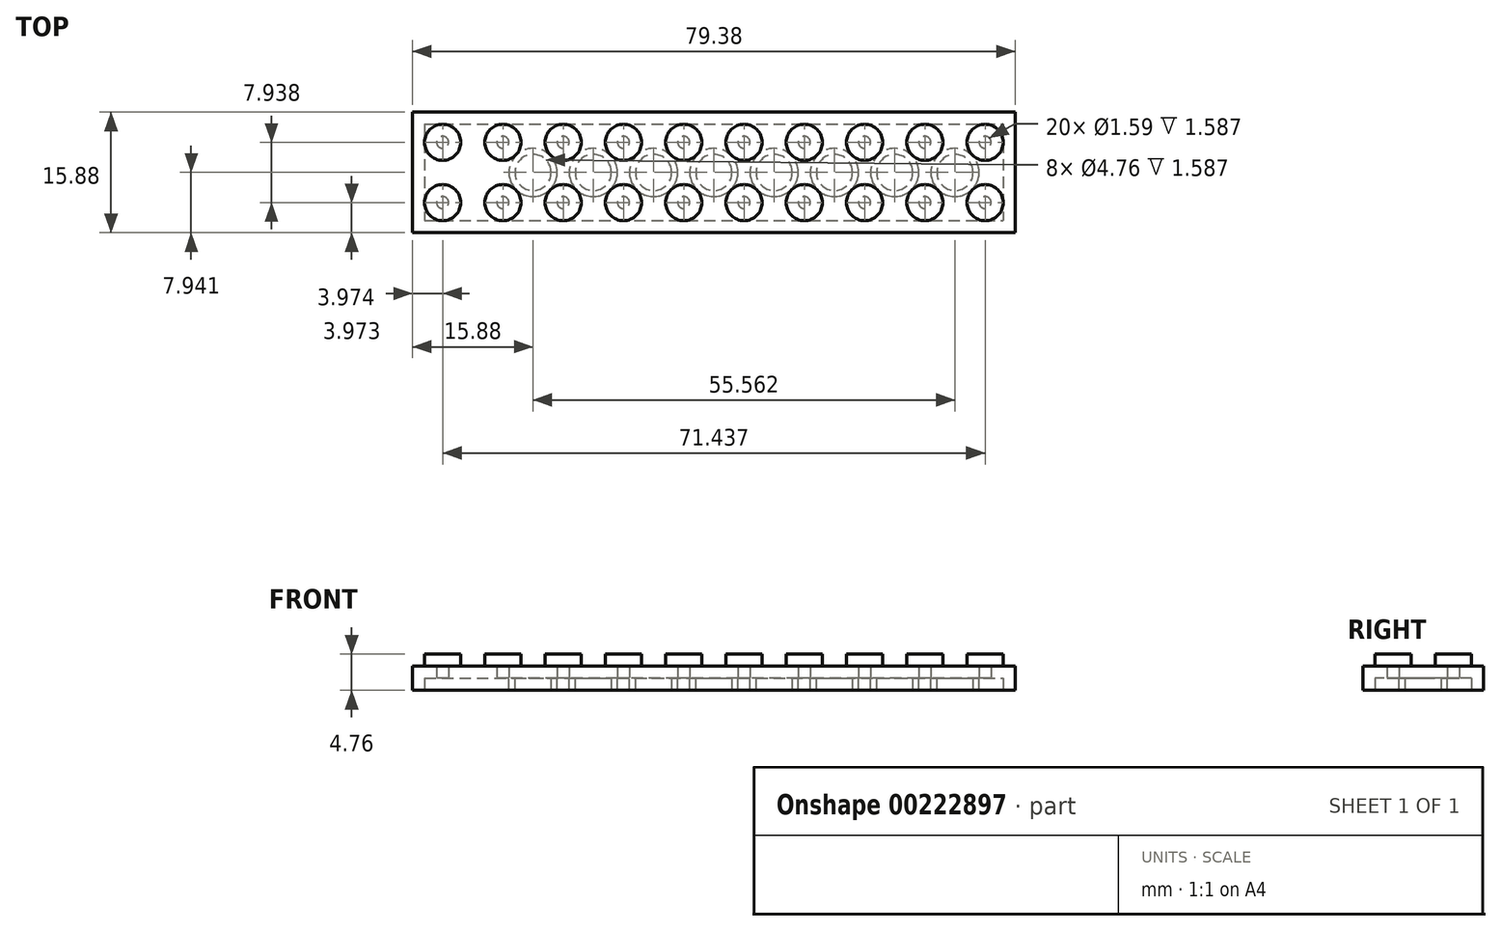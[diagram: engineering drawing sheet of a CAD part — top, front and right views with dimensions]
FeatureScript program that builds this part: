
annotation { "Feature Type Name" : "Feature", "Feature Type Description" : "" }
export const myFeature = defineFeature(function(context is Context, id is Id, definition is map)
    precondition{}
    {
        {
            var Q0;
            Q0=qCreatedBy(makeId("Top.planeOp"),FACE);
            var sketch = newSketch(context, id + "F0", { "sketchPlane" : qUnion([Q0])});
            skLineSegment(sketch, "E0.bottom", {"start": v(-15.88, 3.97) * mm, "end": v(63.5, 3.97) * mm});
            skLineSegment(sketch, "E0.top", {"start": v(-15.88, -11.9) * mm, "end": v(63.5, -11.9) * mm});
            skLineSegment(sketch, "E0.left", {"start": v(-15.88, 3.97) * mm, "end": v(-15.88, -11.9) * mm});
            skLineSegment(sketch, "E0.right", {"start": v(63.5, 3.97) * mm, "end": v(63.5, -11.9) * mm});
            skCircle(sketch, "E1", {"center": v(-11.9, 0) * mm, "radius": 2.38 * mm});
            skCircle(sketch, "E2.0.1.0", {"center": v(-11.9, -7.94) * mm, "radius": 2.38 * mm});
            skCircle(sketch, "E2.1.0.0", {"center": v(-3.97, 0) * mm, "radius": 2.38 * mm});
            skCircle(sketch, "E2.1.1.0", {"center": v(-3.97, -7.94) * mm, "radius": 2.38 * mm});
            skCircle(sketch, "E2.2.0.0", {"center": v(3.97, 0) * mm, "radius": 2.38 * mm});
            skCircle(sketch, "E2.2.1.0", {"center": v(3.97, -7.94) * mm, "radius": 2.38 * mm});
            skCircle(sketch, "E2.3.0.0", {"center": v(11.9, 0) * mm, "radius": 2.38 * mm});
            skCircle(sketch, "E2.3.1.0", {"center": v(11.9, -7.94) * mm, "radius": 2.38 * mm});
            skLineSegment(sketch, "E2.direction1", {"start": v(-11.9, 0) * mm, "end": v(-3.97, 0) * mm, "construction": true});
            skLineSegment(sketch, "E2.direction2", {"start": v(-11.9, 0) * mm, "end": v(-11.9, -7.94) * mm, "construction": true});
            skCircle(sketch, "E3.0.4.0", {"center": v(19.84, 0) * mm, "radius": 2.38 * mm});
            skCircle(sketch, "E3.0.4.1", {"center": v(19.84, -7.94) * mm, "radius": 2.38 * mm});
            skCircle(sketch, "E3.0.5.0", {"center": v(27.78, 0) * mm, "radius": 2.38 * mm});
            skCircle(sketch, "E3.0.5.1", {"center": v(27.78, -7.94) * mm, "radius": 2.38 * mm});
            skCircle(sketch, "E4.0.6.0", {"center": v(35.72, 0) * mm, "radius": 2.38 * mm});
            skCircle(sketch, "E4.0.6.1", {"center": v(35.72, -7.94) * mm, "radius": 2.38 * mm});
            skCircle(sketch, "E4.0.7.0", {"center": v(43.66, 0) * mm, "radius": 2.38 * mm});
            skCircle(sketch, "E4.0.7.1", {"center": v(43.66, -7.94) * mm, "radius": 2.38 * mm});
            skCircle(sketch, "E5.0.8.0", {"center": v(51.6, 0) * mm, "radius": 2.38 * mm});
            skCircle(sketch, "E5.0.8.1", {"center": v(51.6, -7.94) * mm, "radius": 2.38 * mm});
            skCircle(sketch, "E5.0.9.0", {"center": v(59.53, 0) * mm, "radius": 2.38 * mm});
            skCircle(sketch, "E5.0.9.1", {"center": v(59.53, -7.94) * mm, "radius": 2.38 * mm});
            skSolve(sketch);
        }
        {
            var Q0;
            Q0=makeQuery(id+"F0.imprint","IMPRINT",FACE,{"disambiguationData":[TD([[makeQuery(id+"F0.imprint","IMPRINT",EDGE,{"derivedFrom":sQuery(id+"F0.wireOp",EDGE,"E0.bottom")}),-1.0]])]});
            extrude(context, id + "F1", {"entities" : qUnion([Q0]), "depth" : 3.17 * mm});
        }
        {
            var Q0;
            Q0=makeQuery(id+"F0.imprint","IMPRINT",FACE,{"disambiguationData":[TD([[makeQuery(id+"F0.imprint","IMPRINT",EDGE,{"derivedFrom":sQuery(id+"F0.wireOp",EDGE,"E1")}),1.0]])]});
            var Q1;
            Q1=makeQuery(id+"F0.imprint","IMPRINT",FACE,{"disambiguationData":[TD([[makeQuery(id+"F0.imprint","IMPRINT",EDGE,{"derivedFrom":sQuery(id+"F0.wireOp",EDGE,"E2.0.1.0")}),1.0]])]});
            var Q2;
            Q2=makeQuery(id+"F0.imprint","IMPRINT",FACE,{"disambiguationData":[TD([[makeQuery(id+"F0.imprint","IMPRINT",EDGE,{"derivedFrom":sQuery(id+"F0.wireOp",EDGE,"E2.1.1.0")}),1.0]])]});
            var Q3;
            Q3=makeQuery(id+"F0.imprint","IMPRINT",FACE,{"disambiguationData":[TD([[makeQuery(id+"F0.imprint","IMPRINT",EDGE,{"derivedFrom":sQuery(id+"F0.wireOp",EDGE,"E2.1.0.0")}),1.0]])]});
            var Q4;
            Q4=makeQuery(id+"F0.imprint","IMPRINT",FACE,{"disambiguationData":[TD([[makeQuery(id+"F0.imprint","IMPRINT",EDGE,{"derivedFrom":sQuery(id+"F0.wireOp",EDGE,"E2.2.0.0")}),1.0]])]});
            var Q5;
            Q5=makeQuery(id+"F0.imprint","IMPRINT",FACE,{"disambiguationData":[TD([[makeQuery(id+"F0.imprint","IMPRINT",EDGE,{"derivedFrom":sQuery(id+"F0.wireOp",EDGE,"E2.2.1.0")}),1.0]])]});
            var Q6;
            Q6=makeQuery(id+"F0.imprint","IMPRINT",FACE,{"disambiguationData":[TD([[makeQuery(id+"F0.imprint","IMPRINT",EDGE,{"derivedFrom":sQuery(id+"F0.wireOp",EDGE,"E2.3.1.0")}),1.0]])]});
            var Q7;
            Q7=makeQuery(id+"F0.imprint","IMPRINT",FACE,{"disambiguationData":[TD([[makeQuery(id+"F0.imprint","IMPRINT",EDGE,{"derivedFrom":sQuery(id+"F0.wireOp",EDGE,"E2.3.0.0")}),1.0]])]});
            var Q8;
            Q8=makeQuery(id+"F0.imprint","IMPRINT",FACE,{"disambiguationData":[TD([[makeQuery(id+"F0.imprint","IMPRINT",EDGE,{"derivedFrom":sQuery(id+"F0.wireOp",EDGE,"E3.0.4.0")}),1.0]])]});
            var Q9;
            Q9=makeQuery(id+"F0.imprint","IMPRINT",FACE,{"disambiguationData":[TD([[makeQuery(id+"F0.imprint","IMPRINT",EDGE,{"derivedFrom":sQuery(id+"F0.wireOp",EDGE,"E3.0.5.0")}),1.0]])]});
            var Q10;
            Q10=makeQuery(id+"F0.imprint","IMPRINT",FACE,{"disambiguationData":[TD([[makeQuery(id+"F0.imprint","IMPRINT",EDGE,{"derivedFrom":sQuery(id+"F0.wireOp",EDGE,"E3.0.5.1")}),1.0]])]});
            var Q11;
            Q11=makeQuery(id+"F0.imprint","IMPRINT",FACE,{"disambiguationData":[TD([[makeQuery(id+"F0.imprint","IMPRINT",EDGE,{"derivedFrom":sQuery(id+"F0.wireOp",EDGE,"E3.0.4.1")}),1.0]])]});
            var Q12;
            Q12=makeQuery(id+"F0.imprint","IMPRINT",FACE,{"disambiguationData":[TD([[makeQuery(id+"F0.imprint","IMPRINT",EDGE,{"derivedFrom":sQuery(id+"F0.wireOp",EDGE,"E4.0.6.0")}),1.0]])]});
            var Q13;
            Q13=makeQuery(id+"F0.imprint","IMPRINT",FACE,{"disambiguationData":[TD([[makeQuery(id+"F0.imprint","IMPRINT",EDGE,{"derivedFrom":sQuery(id+"F0.wireOp",EDGE,"E4.0.7.0")}),1.0]])]});
            var Q14;
            Q14=makeQuery(id+"F0.imprint","IMPRINT",FACE,{"disambiguationData":[TD([[makeQuery(id+"F0.imprint","IMPRINT",EDGE,{"derivedFrom":sQuery(id+"F0.wireOp",EDGE,"E4.0.7.1")}),1.0]])]});
            var Q15;
            Q15=makeQuery(id+"F0.imprint","IMPRINT",FACE,{"disambiguationData":[TD([[makeQuery(id+"F0.imprint","IMPRINT",EDGE,{"derivedFrom":sQuery(id+"F0.wireOp",EDGE,"E4.0.6.1")}),1.0]])]});
            var Q16;
            Q16=makeQuery(id+"F0.imprint","IMPRINT",FACE,{"disambiguationData":[TD([[makeQuery(id+"F0.imprint","IMPRINT",EDGE,{"derivedFrom":sQuery(id+"F0.wireOp",EDGE,"E5.0.8.0")}),1.0]])]});
            var Q17;
            Q17=makeQuery(id+"F0.imprint","IMPRINT",FACE,{"disambiguationData":[TD([[makeQuery(id+"F0.imprint","IMPRINT",EDGE,{"derivedFrom":sQuery(id+"F0.wireOp",EDGE,"E5.0.9.0")}),1.0]])]});
            var Q18;
            Q18=makeQuery(id+"F0.imprint","IMPRINT",FACE,{"disambiguationData":[TD([[makeQuery(id+"F0.imprint","IMPRINT",EDGE,{"derivedFrom":sQuery(id+"F0.wireOp",EDGE,"E5.0.9.1")}),1.0]])]});
            var Q19;
            Q19=makeQuery(id+"F0.imprint","IMPRINT",FACE,{"disambiguationData":[TD([[makeQuery(id+"F0.imprint","IMPRINT",EDGE,{"derivedFrom":sQuery(id+"F0.wireOp",EDGE,"E5.0.8.1")}),1.0]])]});
            extrude(context, id + "F2", {"entities" : qUnion([Q0, Q1, Q2, Q3, Q4, Q5, Q6, Q7, Q8, Q9, Q10, Q11, Q12, Q13, Q14, Q15, Q16, Q17, Q18, Q19]), "operationType" : NewBodyOperationType.ADD, "depth" : 4.76 * mm});
        }
        {
            var Q0;
            {var subQ0=sQuery(id+"F0.wireOp",EDGE,"8b71ed98-f0e1-4300-85cb-82ad82c44b3e0.MirrorC");var subQ1=sQuery(id+"F0.wireOp",EDGE,"E1");Q0=makeQuery(id+"F2.boolean.opBoolean","MERGE",FACE,{"derivedFrom":[makeQuery(id+"F1.opExtrude","CAP_FACE",FACE,{"disambiguationData":[OSD([sQuery(id+"F0.wireOp",EDGE,"E0.bottom"),sQuery(id+"F0.wireOp",EDGE,"E0.top"),sQuery(id+"F0.wireOp",EDGE,"E0.left"),sQuery(id+"F0.wireOp",EDGE,"E0.right"),subQ1,subQ0])],"isStart":true}),makeQuery(id+"F2.opExtrude","CAP_FACE",FACE,{"disambiguationData":[OSD([subQ1])],"isStart":true}),makeQuery(id+"F2.opExtrude","CAP_FACE",FACE,{"disambiguationData":[OSD([subQ0])],"isStart":true})]});}
            shell(context, id + "F3", {"entities" : qUnion([Q0]), "thickness" : 1.59 * mm});
        }
        {
            var Q0;
            Q0=makeQuery(id+"F3.opShell","OFFSET_FACE",FACE,{"disambiguationData":[OSD([sQuery(id+"F0.wireOp",EDGE,"E0.bottom"),sQuery(id+"F0.wireOp",EDGE,"E0.top"),sQuery(id+"F0.wireOp",EDGE,"E0.left"),sQuery(id+"F0.wireOp",EDGE,"E0.right"),sQuery(id+"F0.wireOp",EDGE,"E1"),sQuery(id+"F0.wireOp",EDGE,"E2.0.1.0"),sQuery(id+"F0.wireOp",EDGE,"E2.1.0.0"),sQuery(id+"F0.wireOp",EDGE,"E2.1.1.0"),sQuery(id+"F0.wireOp",EDGE,"E2.2.0.0"),sQuery(id+"F0.wireOp",EDGE,"E2.2.1.0"),sQuery(id+"F0.wireOp",EDGE,"E2.3.0.0"),sQuery(id+"F0.wireOp",EDGE,"E2.3.1.0")])]});
            var sketch = newSketch(context, id + "F4", { "sketchPlane" : qUnion([Q0])});
            skLineSegment(sketch, "E6", {"start": v(-11.9, 7.94) * mm, "end": v(-3.97, 0) * mm});
            skCircle(sketch, "E7", {"center": v(-7.94, 3.97) * mm, "radius": 3.18 * mm});
            skCircle(sketch, "E8.0", {"center": v(-7.94, 3.97) * mm, "radius": 2.38 * mm});
            skCircle(sketch, "E9.1.0.0", {"center": v(0, 3.97) * mm, "radius": 3.18 * mm});
            skCircle(sketch, "E9.1.0.1", {"center": v(0, 3.97) * mm, "radius": 2.38 * mm});
            skCircle(sketch, "E9.2.0.0", {"center": v(7.94, 3.97) * mm, "radius": 3.18 * mm});
            skCircle(sketch, "E9.2.0.1", {"center": v(7.94, 3.97) * mm, "radius": 2.38 * mm});
            skLineSegment(sketch, "E9.direction1", {"start": v(-7.94, 3.97) * mm, "end": v(0, 3.97) * mm, "construction": true});
            skCircle(sketch, "E10.0.3.0", {"center": v(15.88, 3.97) * mm, "radius": 3.18 * mm});
            skCircle(sketch, "E10.2.3.0", {"center": v(15.88, 3.97) * mm, "radius": 2.38 * mm});
            skCircle(sketch, "E10.0.4.0", {"center": v(23.81, 3.97) * mm, "radius": 3.18 * mm});
            skCircle(sketch, "E10.2.4.0", {"center": v(23.81, 3.97) * mm, "radius": 2.38 * mm});
            skCircle(sketch, "E11.0.5.0", {"center": v(31.75, 3.97) * mm, "radius": 3.18 * mm});
            skCircle(sketch, "E11.2.5.0", {"center": v(31.75, 3.97) * mm, "radius": 2.38 * mm});
            skCircle(sketch, "E11.0.6.0", {"center": v(39.69, 3.97) * mm, "radius": 3.18 * mm});
            skCircle(sketch, "E11.2.6.0", {"center": v(39.69, 3.97) * mm, "radius": 2.38 * mm});
            skCircle(sketch, "E12.0.7.0", {"center": v(47.62, 3.97) * mm, "radius": 3.18 * mm});
            skCircle(sketch, "E12.2.7.0", {"center": v(47.62, 3.97) * mm, "radius": 2.38 * mm});
            skCircle(sketch, "E12.0.8.0", {"center": v(55.56, 3.97) * mm, "radius": 3.18 * mm});
            skCircle(sketch, "E12.2.8.0", {"center": v(55.56, 3.97) * mm, "radius": 2.38 * mm});
            skSolve(sketch);
        }
        {
            var Q0;
            {var subQ0=sQuery(id+"F4.wireOp",EDGE,"E7");var subQ1=sQuery(id+"F4.wireOp",EDGE,"E6");var subQ2=makeQuery(id+"F4.imprint","INTERSECT",VERTEX,{"disambiguationData":[OD(0.0)],"derivedFrom":[subQ1,subQ0]});Q0=makeQuery(id+"F4.imprint","IMPRINT",FACE,{"disambiguationData":[TD([[makeQuery(id+"F4.imprint","IMPRINT",EDGE,{"disambiguationData":[TD([[subQ2,-1.0]])],"derivedFrom":subQ1}),1.0]])]});}
            var Q1;
            {var subQ0=sQuery(id+"F4.wireOp",EDGE,"E7");var subQ1=sQuery(id+"F4.wireOp",EDGE,"E6");var subQ2=makeQuery(id+"F4.imprint","INTERSECT",VERTEX,{"disambiguationData":[OD(0.0)],"derivedFrom":[subQ1,subQ0]});Q1=makeQuery(id+"F4.imprint","IMPRINT",FACE,{"disambiguationData":[TD([[makeQuery(id+"F4.imprint","IMPRINT",EDGE,{"disambiguationData":[TD([[subQ2,-1.0]])],"derivedFrom":subQ1}),-1.0]])]});}
            var Q2;
            Q2=makeQuery(id+"F4.imprint","IMPRINT",FACE,{"disambiguationData":[TD([[makeQuery(id+"F4.imprint","IMPRINT",EDGE,{"derivedFrom":sQuery(id+"F4.wireOp",EDGE,"E9.1.0.0")}),1.0]])]});
            var Q3;
            Q3=makeQuery(id+"F4.imprint","IMPRINT",FACE,{"disambiguationData":[TD([[makeQuery(id+"F4.imprint","IMPRINT",EDGE,{"derivedFrom":sQuery(id+"F4.wireOp",EDGE,"E9.2.0.0")}),1.0]])]});
            var Q4;
            Q4=makeQuery(id+"F4.imprint","IMPRINT",FACE,{"disambiguationData":[TD([[makeQuery(id+"F4.imprint","IMPRINT",EDGE,{"derivedFrom":sQuery(id+"F4.wireOp",EDGE,"E10.0.3.0")}),1.0]])]});
            var Q5;
            Q5=makeQuery(id+"F4.imprint","IMPRINT",FACE,{"disambiguationData":[TD([[makeQuery(id+"F4.imprint","IMPRINT",EDGE,{"derivedFrom":sQuery(id+"F4.wireOp",EDGE,"E10.0.4.0")}),1.0]])]});
            var Q6;
            Q6=makeQuery(id+"F4.imprint","IMPRINT",FACE,{"disambiguationData":[TD([[makeQuery(id+"F4.imprint","IMPRINT",EDGE,{"derivedFrom":sQuery(id+"F4.wireOp",EDGE,"E11.0.5.0")}),1.0]])]});
            var Q7;
            Q7=makeQuery(id+"F4.imprint","IMPRINT",FACE,{"disambiguationData":[TD([[makeQuery(id+"F4.imprint","IMPRINT",EDGE,{"derivedFrom":sQuery(id+"F4.wireOp",EDGE,"E11.0.6.0")}),1.0]])]});
            var Q8;
            Q8=makeQuery(id+"F4.imprint","IMPRINT",FACE,{"disambiguationData":[TD([[makeQuery(id+"F4.imprint","IMPRINT",EDGE,{"derivedFrom":sQuery(id+"F4.wireOp",EDGE,"E12.0.7.0")}),1.0]])]});
            var Q9;
            Q9=makeQuery(id+"F4.imprint","IMPRINT",FACE,{"disambiguationData":[TD([[makeQuery(id+"F4.imprint","IMPRINT",EDGE,{"derivedFrom":sQuery(id+"F4.wireOp",EDGE,"E12.0.8.0")}),1.0]])]});
            extrude(context, id + "F5", {"entities" : qUnion([Q0, Q1, Q2, Q3, Q4, Q5, Q6, Q7, Q8, Q9]), "operationType" : NewBodyOperationType.ADD, "depth" : 1.59 * mm});
        }
    });
